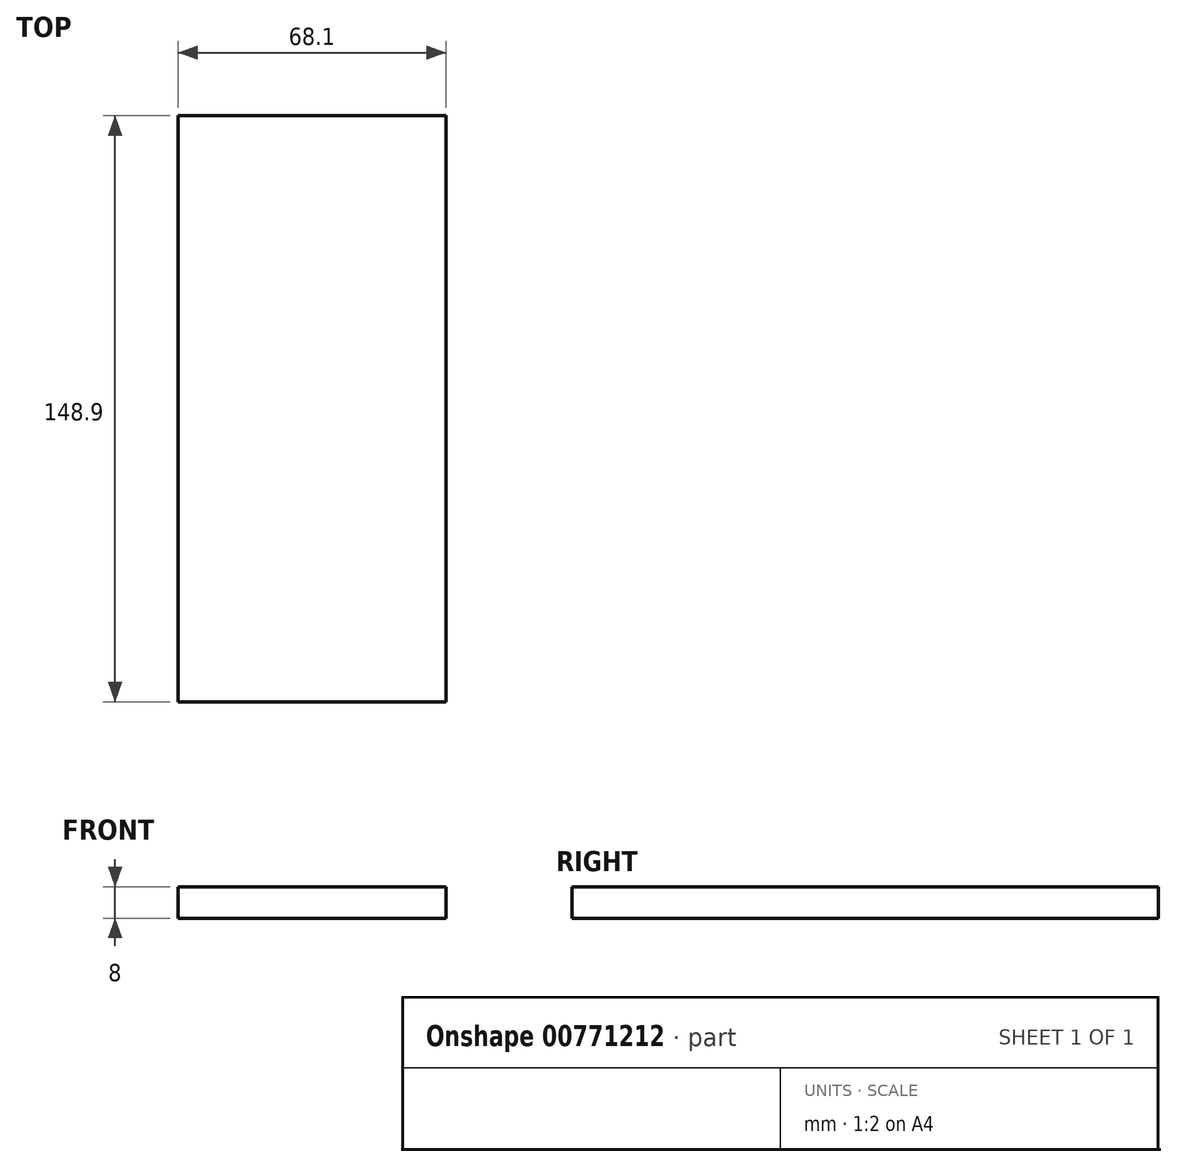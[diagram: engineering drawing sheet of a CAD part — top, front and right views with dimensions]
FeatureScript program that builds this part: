
annotation { "Feature Type Name" : "Feature", "Feature Type Description" : "" }
export const myFeature = defineFeature(function(context is Context, id is Id, definition is map)
    precondition{}
    {
        {
            var Q0;
            Q0=qCreatedBy(makeId("Top.planeOp"),FACE);
            var sketch = newSketch(context, id + "F0", { "sketchPlane" : qUnion([Q0])});
            skLineSegment(sketch, "E0.bottom", {"start": v(-34.05, 74.45) * mm, "end": v(34.05, 74.45) * mm});
            skLineSegment(sketch, "E0.top", {"start": v(-34.05, -74.45) * mm, "end": v(34.05, -74.45) * mm});
            skLineSegment(sketch, "E0.left", {"start": v(-34.05, 74.45) * mm, "end": v(-34.05, -74.45) * mm});
            skLineSegment(sketch, "E0.right", {"start": v(34.05, 74.45) * mm, "end": v(34.05, -74.45) * mm});
            skPoint(sketch, "E0.middle", {"position": v(0, 0) * mm});
            skSolve(sketch);
        }
        {
            var Q0;
            Q0=makeQuery(id+"F0.imprint","IMPRINT",FACE,{"disambiguationData":[TD([[makeQuery(id+"F0.imprint","IMPRINT",EDGE,{"derivedFrom":sQuery(id+"F0.wireOp",EDGE,"E0.bottom")}),-1.0]])]});
            extrude(context, id + "F1", {"entities" : qUnion([Q0]), "depth" : 8 * mm, "offsetDistance" : 25 * mm});
        }
    });
